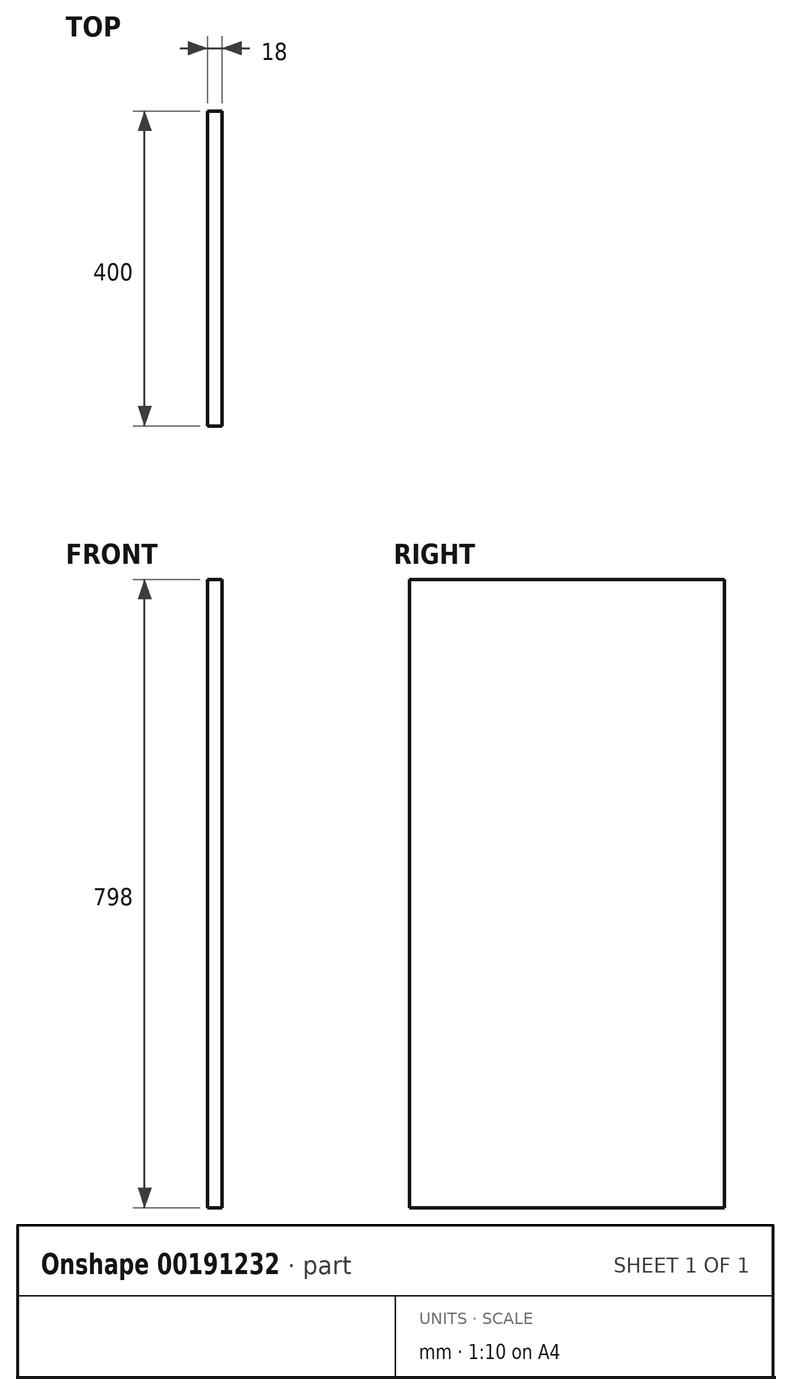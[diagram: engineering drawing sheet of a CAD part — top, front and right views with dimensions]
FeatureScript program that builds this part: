
annotation { "Feature Type Name" : "Feature", "Feature Type Description" : "" }
export const myFeature = defineFeature(function(context is Context, id is Id, definition is map)
    precondition{}
    {
        {
            var Q0;
            Q0=qCreatedBy(makeId("Right.planeOp"),FACE);
            var sketch = newSketch(context, id + "F0", { "sketchPlane" : qUnion([Q0])});
            skLineSegment(sketch, "E0.bottom", {"start": v(0, 0) * mm, "end": v(400, 0) * mm});
            skLineSegment(sketch, "E0.top", {"start": v(0, 798) * mm, "end": v(400, 798) * mm});
            skLineSegment(sketch, "E0.left", {"start": v(0, 0) * mm, "end": v(0, 798) * mm});
            skLineSegment(sketch, "E0.right", {"start": v(400, 0) * mm, "end": v(400, 798) * mm});
            skSolve(sketch);
        }
        {
            var Q0;
            Q0 = qSketchRegion(id + "F0", true);
            extrude(context, id + "F1", {"entities" : qUnion([Q0]), "depth" : 18 * mm});
        }
    });
